# Revit family: Edge_TB42_C_Side_Hung_Standard
name_source: partatom
category: Windows
revit_build: Autodesk Revit 2014 (Build: 20130308_1515(x64)
units: mm (PartAtom-declared; Revit-internal decimal feet)

## types (12) — shared parameters
Aluminium Thickness = 1 mm  [stored 0.00328084 ft]
Bead SG Gap = 13 mm
Casement Dimension = 42 mm  [stored 0.137795 ft]
Custom Sash Left Width = 554 mm  [stored 1.81759 ft]
Custom Sash Right Width = 554 mm  [stored 1.81759 ft]
DG Extrusion Start = 11 mm  [stored 0.0360892 ft]
DG Gasket Finish = Double Glazing Gasket Material
DG Thickness Calc = 4 mm  [stored 0.0131234 ft]
Default Sill Height = 800 mm  [stored 2.62467 ft]
Depth Bead = 28 mm  [stored 0.0918635 ft]
Depth Mullion = 43 mm  [stored 0.141076 ft]
Description = Thermal break casement windows (42mm), Type C side hung
Frame Center Offset = 21 mm  [stored 0.0688976 ft]
Limit Fixed Pane Width Max = 1500 mm  [stored 4.92126 ft]
Limit Fixed Pane Width Min = 200 mm  [stored 0.656168 ft]
Limit Sash Height Max = 1500 mm  [stored 4.92126 ft]
Limit Sash Height Min = 300 mm  [stored 0.984252 ft]
Limit Sash Width Max = 700 mm  [stored 2.29659 ft]
Limit Sash Width Min = 300 mm  [stored 0.984252 ft]
Limit Window Height Max = 1546 mm
Limit Window Height Min = 346 mm
Limit Window Width Max = 2700 mm
Limit Window Width Min = 1400 mm
Manufacturer = Crealco
Max System DG One Piece Thickness = 6 mm  [stored 0.019685 ft]
Max System DG Unit Thickness = 25 mm  [stored 0.082021 ft]
Model = Edge
Offset Bead Center Reversed = 21 mm  [stored 0.0688976 ft]
Offset Fixed Panel Left = 600 mm  [stored 1.9685 ft]
Offset Mullion Left Side = 570 mm  [stored 1.87008 ft]
Offset Mullion Right Side = 570 mm  [stored 1.87008 ft]
Offset Sash Side = 23 mm  [stored 0.0754593 ft]
Offset Sash Top = 23 mm  [stored 0.0754593 ft]
Offset Window Exterior = 21 mm  [stored 0.0688976 ft]
SG Gasket Thickness = 6 mm  [stored 0.019685 ft]
Sash Center Offset = 18 mm
Sash Overlap = 7 mm  [stored 0.0229659 ft]
Sash Spacing Inner = 8 mm  [stored 0.0262467 ft]
Side Hung Left = Yes
Side Hung Right = No
URL = http://www.crealco.co.za
Wall Closure = By host
Width Bead = 15 mm  [stored 0.0492126 ft]
Width Profile = 30 mm  [stored 0.0984252 ft]
Width Sash Left = 554 mm  [stored 1.81759 ft]
Width Sash Left Opening = 524 mm  [stored 1.71916 ft]
Width Sash Right = 554 mm  [stored 1.81759 ft]
Width Sash Right Opening = 524 mm  [stored 1.71916 ft]
zero-valued in all types: Window Exterior Offset

## per-type parameters (varying)
- EDGE-1809SS-1000Pa: Area Pane Left=0.35 m²; Area Pane Middle=0.48 m²; Area Pane Right=0.35 m²; Clearvue Insulated LowE SHGC Value=0.461; Clearvue Insulated LowE U Value=2.6; Clearvue Insulated SHGC Value=0.507; Clearvue Insulated U Value=3.09; Clearvue SHGC Value=0.564; Clearvue U Value=5.33; Custom Windload=1000 mm  [stored 3.28084 ft]; Custom Window Height=890 mm  [stored 2.91995 ft]; Custom Window Width=1790 mm; Energy Advantage SHGC Value=0.505; Energy Advantage U Value=3.96; Has Stiffener Cap=No; Height=890 mm  [stored 2.91995 ft]; Height Fixed Panel Center=830 mm  [stored 2.7231 ft]; Height Sash=814 mm  [stored 2.6706 ft]; Height Sash Opening=844 mm  [stored 2.76903 ft]; Intruderprufe Insulated LowE SHGC Value=0.419; Intruderprufe Insulated LowE U Value=2.56; Intruderprufe Insulated SHGC Value=0.465; Intruderprufe Insulated U Value=3.05; Intruderprufe LowE SHGC Value=0.471; Intruderprufe LowE U Value=3.96; Intruderprufe SHGC Value=0.526; Intruderprufe U Value=5.24; Length Mullion=890 mm  [stored 2.91995 ft]; Max Pane Area=0.48 m²; Mullion Depth Windload Based=0 mm  [stored 0 ft]; Sash Height=845 mm  [stored 2.77231 ft]; Width=1790 mm; Width Fixed Panel Center=590 mm; Windload Design=1000 mm  [stored 3.28084 ft]
- EDGE-2409SS-1000Pa: Area Pane Left=0.35 m²; Area Pane Middle=0.97 m²; Area Pane Right=0.35 m²; Clearvue Insulated LowE SHGC Value=0.499; Clearvue Insulated LowE U Value=2.49; Clearvue Insulated SHGC Value=0.549; Clearvue Insulated U Value=3.03; Clearvue SHGC Value=0.612; Clearvue U Value=5.43; Custom Windload=1000 mm  [stored 3.28084 ft]; Custom Window Height=890 mm  [stored 2.91995 ft]; Custom Window Width=2390 mm; Energy Advantage SHGC Value=0.548; Energy Advantage U Value=3.92; Has Stiffener Cap=No; Height=890 mm  [stored 2.91995 ft]; Height Fixed Panel Center=830 mm  [stored 2.7231 ft]; Height Sash=814 mm  [stored 2.6706 ft]; Height Sash Opening=844 mm  [stored 2.76903 ft]; Intruderprufe Insulated LowE SHGC Value=0.455; Intruderprufe Insulated LowE U Value=2.45; Intruderprufe Insulated SHGC Value=0.504; Intruderprufe Insulated U Value=2.98; Intruderprufe LowE SHGC Value=0.511; Intruderprufe LowE U Value=3.91; Intruderprufe SHGC Value=0.572; Intruderprufe U Value=5.3; Length Mullion=890 mm  [stored 2.91995 ft]; Max Pane Area=0.97 m²; Mullion Depth Windload Based=0 mm  [stored 0 ft]; Sash Height=845 mm  [stored 2.77231 ft]; Width=2390 mm; Width Fixed Panel Center=1190 mm  [stored 3.9042 ft]; Windload Design=1000 mm  [stored 3.28084 ft]
- EDGE-1812SS-1000Pa: Area Pane Left=0.49 m²; Area Pane Middle=0.65 m²; Area Pane Right=0.49 m²; Clearvue Insulated LowE SHGC Value=0.481; Clearvue Insulated LowE U Value=2.54; Clearvue Insulated SHGC Value=0.529; Clearvue Insulated U Value=6.05; Clearvue SHGC Value=0.591; Clearvue U Value=5.38; Custom Windload=1000 mm  [stored 3.28084 ft]; Custom Window Height=1190 mm  [stored 3.9042 ft]; Custom Window Width=1790 mm; Energy Advantage SHGC Value=0.528; Energy Advantage U Value=3.94; Has Stiffener Cap=No; Height=1190 mm  [stored 3.9042 ft]; Height Fixed Panel Center=1130 mm  [stored 3.70735 ft]; Height Sash=1114 mm  [stored 3.65486 ft]; Height Sash Opening=1144 mm  [stored 3.75328 ft]; Intruderprufe Insulated LowE SHGC Value=0.486; Intruderprufe Insulated LowE U Value=3.01; Intruderprufe Insulated SHGC Value=0.438; Intruderprufe Insulated U Value=2.5; Intruderprufe LowE SHGC Value=0.493; Intruderprufe LowE U Value=3.93; Intruderprufe SHGC Value=0.552; Intruderprufe U Value=5.29; Length Mullion=1190 mm  [stored 3.9042 ft]; Max Pane Area=0.65 m²; Mullion Depth Windload Based=0 mm  [stored 0 ft]; Sash Height=1145 mm  [stored 3.75656 ft]; Width=1790 mm; Width Fixed Panel Center=590 mm; Windload Design=1000 mm  [stored 3.28084 ft]
- EDGE-2412SS-1000Pa: Area Pane Left=0.49 m²; Area Pane Middle=1.32 m²; Area Pane Right=0.49 m²; Clearvue Insulated LowE SHGC Value=0.519; Clearvue Insulated LowE U Value=2.42; Clearvue Insulated SHGC Value=0.57; Clearvue Insulated U Value=2.99; Clearvue SHGC Value=0.638; Clearvue U Value=5.48; Custom Windload=1000 mm  [stored 3.28084 ft]; Custom Window Height=1190 mm  [stored 3.9042 ft]; Custom Window Width=2390 mm; Energy Advantage SHGC Value=0.571; Energy Advantage U Value=3.9; Has Stiffener Cap=No; Height=1190 mm  [stored 3.9042 ft]; Height Fixed Panel Center=1130 mm  [stored 3.70735 ft]; Height Sash=1114 mm  [stored 3.65486 ft]; Height Sash Opening=1144 mm  [stored 3.75328 ft]; Intruderprufe Insulated LowE SHGC Value=0.473; Intruderprufe Insulated LowE U Value=2.39; Intruderprufe Insulated SHGC Value=0.524; Intruderprufe Insulated U Value=2.95; Intruderprufe LowE SHGC Value=0.532; Intruderprufe LowE U Value=3.88; Intruderprufe SHGC Value=0.597; Intruderprufe U Value=5.38; Length Mullion=1190 mm  [stored 3.9042 ft]; Max Pane Area=1.32 m²; Mullion Depth Windload Based=0 mm  [stored 0 ft]; Sash Height=1145 mm  [stored 3.75656 ft]; Width=2390 mm; Width Fixed Panel Center=1190 mm  [stored 3.9042 ft]; Windload Design=1000 mm  [stored 3.28084 ft]
- EDGE-1809SS-1500Pa: Area Pane Left=0.35 m²; Area Pane Middle=0.48 m²; Area Pane Right=0.35 m²; Clearvue Insulated LowE SHGC Value=0.461; Clearvue Insulated LowE U Value=2.6; Clearvue Insulated SHGC Value=0.507; Clearvue Insulated U Value=3.09; Clearvue SHGC Value=0.564; Clearvue U Value=5.33; Custom Windload=1500 mm  [stored 4.92126 ft]; Custom Window Height=890 mm  [stored 2.91995 ft]; Custom Window Width=1790 mm; Energy Advantage SHGC Value=0.505; Energy Advantage U Value=3.96; Has Stiffener Cap=No; Height=890 mm  [stored 2.91995 ft]; Height Fixed Panel Center=830 mm  [stored 2.7231 ft]; Height Sash=814 mm  [stored 2.6706 ft]; Height Sash Opening=844 mm  [stored 2.76903 ft]; Intruderprufe Insulated LowE SHGC Value=0.419; Intruderprufe Insulated LowE U Value=2.56; Intruderprufe Insulated SHGC Value=0.465; Intruderprufe Insulated U Value=3.05; Intruderprufe LowE SHGC Value=0.471; Intruderprufe LowE U Value=3.96; Intruderprufe SHGC Value=0.526; Intruderprufe U Value=5.24; Length Mullion=890 mm  [stored 2.91995 ft]; Max Pane Area=0.48 m²; Mullion Depth Windload Based=0 mm  [stored 0 ft]; Sash Height=845 mm  [stored 2.77231 ft]; Width=1790 mm; Width Fixed Panel Center=590 mm; Windload Design=1500 mm  [stored 4.92126 ft]
- EDGE-1809SS-2000Pa: Area Pane Left=0.35 m²; Area Pane Middle=0.48 m²; Area Pane Right=0.35 m²; Clearvue Insulated LowE SHGC Value=0.461; Clearvue Insulated LowE U Value=2.6; Clearvue Insulated SHGC Value=0.507; Clearvue Insulated U Value=3.09; Clearvue SHGC Value=0.564; Clearvue U Value=5.33; Custom Windload=2000 mm; Custom Window Height=890 mm  [stored 2.91995 ft]; Custom Window Width=1790 mm; Energy Advantage SHGC Value=0.505; Energy Advantage U Value=3.96; Has Stiffener Cap=No; Height=890 mm  [stored 2.91995 ft]; Height Fixed Panel Center=830 mm  [stored 2.7231 ft]; Height Sash=814 mm  [stored 2.6706 ft]; Height Sash Opening=844 mm  [stored 2.76903 ft]; Intruderprufe Insulated LowE SHGC Value=0.419; Intruderprufe Insulated LowE U Value=2.56; Intruderprufe Insulated SHGC Value=0.465; Intruderprufe Insulated U Value=3.05; Intruderprufe LowE SHGC Value=0.471; Intruderprufe LowE U Value=3.96; Intruderprufe SHGC Value=0.526; Intruderprufe U Value=5.24; Length Mullion=890 mm  [stored 2.91995 ft]; Max Pane Area=0.48 m²; Mullion Depth Windload Based=0 mm  [stored 0 ft]; Sash Height=845 mm  [stored 2.77231 ft]; Width=1790 mm; Width Fixed Panel Center=590 mm; Windload Design=2000 mm
- EDGE-2409SS-1500Pa: Area Pane Left=0.35 m²; Area Pane Middle=0.97 m²; Area Pane Right=0.35 m²; Clearvue Insulated LowE SHGC Value=0.499; Clearvue Insulated LowE U Value=2.49; Clearvue Insulated SHGC Value=0.549; Clearvue Insulated U Value=3.03; Clearvue SHGC Value=0.612; Clearvue U Value=5.43; Custom Windload=1500 mm  [stored 4.92126 ft]; Custom Window Height=890 mm  [stored 2.91995 ft]; Custom Window Width=2390 mm; Energy Advantage SHGC Value=0.548; Energy Advantage U Value=3.92; Has Stiffener Cap=No; Height=890 mm  [stored 2.91995 ft]; Height Fixed Panel Center=830 mm  [stored 2.7231 ft]; Height Sash=814 mm  [stored 2.6706 ft]; Height Sash Opening=844 mm  [stored 2.76903 ft]; Intruderprufe Insulated LowE SHGC Value=0.455; Intruderprufe Insulated LowE U Value=2.45; Intruderprufe Insulated SHGC Value=0.504; Intruderprufe Insulated U Value=2.98; Intruderprufe LowE SHGC Value=0.511; Intruderprufe LowE U Value=3.91; Intruderprufe SHGC Value=0.572; Intruderprufe U Value=5.3; Length Mullion=890 mm  [stored 2.91995 ft]; Max Pane Area=0.97 m²; Mullion Depth Windload Based=0 mm  [stored 0 ft]; Sash Height=845 mm  [stored 2.77231 ft]; Width=2390 mm; Width Fixed Panel Center=1190 mm  [stored 3.9042 ft]; Windload Design=1500 mm  [stored 4.92126 ft]
- EDGE-2409SS-2000Pa: Area Pane Left=0.35 m²; Area Pane Middle=0.97 m²; Area Pane Right=0.35 m²; Clearvue Insulated LowE SHGC Value=0.499; Clearvue Insulated LowE U Value=2.49; Clearvue Insulated SHGC Value=0.549; Clearvue Insulated U Value=3.03; Clearvue SHGC Value=0.612; Clearvue U Value=5.43; Custom Windload=2000 mm; Custom Window Height=890 mm  [stored 2.91995 ft]; Custom Window Width=2390 mm; Energy Advantage SHGC Value=0.548; Energy Advantage U Value=3.92; Has Stiffener Cap=No; Height=890 mm  [stored 2.91995 ft]; Height Fixed Panel Center=830 mm  [stored 2.7231 ft]; Height Sash=814 mm  [stored 2.6706 ft]; Height Sash Opening=844 mm  [stored 2.76903 ft]; Intruderprufe Insulated LowE SHGC Value=0.455; Intruderprufe Insulated LowE U Value=2.45; Intruderprufe Insulated SHGC Value=0.504; Intruderprufe Insulated U Value=2.98; Intruderprufe LowE SHGC Value=0.511; Intruderprufe LowE U Value=3.91; Intruderprufe SHGC Value=0.572; Intruderprufe U Value=5.3; Length Mullion=890 mm  [stored 2.91995 ft]; Max Pane Area=0.97 m²; Mullion Depth Windload Based=0 mm  [stored 0 ft]; Sash Height=845 mm  [stored 2.77231 ft]; Width=2390 mm; Width Fixed Panel Center=1190 mm  [stored 3.9042 ft]; Windload Design=2000 mm
- EDGE-1812SS-1500Pa: Area Pane Left=0.49 m²; Area Pane Middle=0.65 m²; Area Pane Right=0.49 m²; Clearvue Insulated LowE SHGC Value=0.481; Clearvue Insulated LowE U Value=2.54; Clearvue Insulated SHGC Value=0.529; Clearvue Insulated U Value=6.05; Clearvue SHGC Value=0.591; Clearvue U Value=5.38; Custom Windload=1500 mm  [stored 4.92126 ft]; Custom Window Height=1190 mm  [stored 3.9042 ft]; Custom Window Width=1790 mm; Energy Advantage SHGC Value=0.528; Energy Advantage U Value=3.94; Has Stiffener Cap=No; Height=1190 mm  [stored 3.9042 ft]; Height Fixed Panel Center=1130 mm  [stored 3.70735 ft]; Height Sash=1114 mm  [stored 3.65486 ft]; Height Sash Opening=1144 mm  [stored 3.75328 ft]; Intruderprufe Insulated LowE SHGC Value=0.486; Intruderprufe Insulated LowE U Value=3.01; Intruderprufe Insulated SHGC Value=0.438; Intruderprufe Insulated U Value=2.5; Intruderprufe LowE SHGC Value=0.493; Intruderprufe LowE U Value=3.93; Intruderprufe SHGC Value=0.552; Intruderprufe U Value=5.29; Length Mullion=1190 mm  [stored 3.9042 ft]; Max Pane Area=0.65 m²; Mullion Depth Windload Based=0 mm  [stored 0 ft]; Sash Height=1145 mm  [stored 3.75656 ft]; Width=1790 mm; Width Fixed Panel Center=590 mm; Windload Design=1500 mm  [stored 4.92126 ft]
- EDGE-1812SS-2000Pa: Area Pane Left=0.49 m²; Area Pane Middle=0.65 m²; Area Pane Right=0.49 m²; Clearvue Insulated LowE SHGC Value=0.551; Clearvue Insulated LowE U Value=2.07; Clearvue Insulated SHGC Value=0.606; Clearvue Insulated U Value=2.6; Clearvue SHGC Value=0.678; Clearvue U Value=4.79; Custom Windload=2000 mm; Custom Window Height=1190 mm  [stored 3.9042 ft]; Custom Window Width=1790 mm; Energy Advantage SHGC Value=0.605; Energy Advantage U Value=3.35; Has Stiffener Cap=Yes; Height=1190 mm  [stored 3.9042 ft]; Height Fixed Panel Center=1130 mm  [stored 3.70735 ft]; Height Sash=1114 mm  [stored 3.65486 ft]; Height Sash Opening=1144 mm  [stored 3.75328 ft]; Intruderprufe Insulated LowE SHGC Value=0.502; Intruderprufe Insulated LowE U Value=2.03; Intruderprufe Insulated SHGC Value=0.558; Intruderprufe Insulated U Value=2.55; Intruderprufe LowE SHGC Value=0.564; Intruderprufe LowE U Value=3.32; Intruderprufe SHGC Value=0.635; Intruderprufe U Value=4.7; Length Mullion=1190 mm  [stored 3.9042 ft]; Max Pane Area=0.65 m²; Mullion Depth Windload Based=1 mm  [stored 0.00328084 ft]; Sash Height=1145 mm  [stored 3.75656 ft]; Width=1790 mm; Width Fixed Panel Center=590 mm; Windload Design=2000 mm
- EDGE-2412SS-1500Pa: Area Pane Left=0.49 m²; Area Pane Middle=1.32 m²; Area Pane Right=0.49 m²; Clearvue Insulated LowE SHGC Value=0.519; Clearvue Insulated LowE U Value=2.42; Clearvue Insulated SHGC Value=0.57; Clearvue Insulated U Value=2.99; Clearvue SHGC Value=0.638; Clearvue U Value=5.48; Custom Windload=1500 mm  [stored 4.92126 ft]; Custom Window Height=1190 mm  [stored 3.9042 ft]; Custom Window Width=2390 mm; Energy Advantage SHGC Value=0.571; Energy Advantage U Value=3.9; Has Stiffener Cap=No; Height=1190 mm  [stored 3.9042 ft]; Height Fixed Panel Center=1130 mm  [stored 3.70735 ft]; Height Sash=1114 mm  [stored 3.65486 ft]; Height Sash Opening=1144 mm  [stored 3.75328 ft]; Intruderprufe Insulated LowE SHGC Value=0.473; Intruderprufe Insulated LowE U Value=2.39; Intruderprufe Insulated SHGC Value=0.524; Intruderprufe Insulated U Value=2.95; Intruderprufe LowE SHGC Value=0.532; Intruderprufe LowE U Value=3.88; Intruderprufe SHGC Value=0.597; Intruderprufe U Value=5.38; Length Mullion=1190 mm  [stored 3.9042 ft]; Max Pane Area=1.32 m²; Mullion Depth Windload Based=0 mm  [stored 0 ft]; Sash Height=1145 mm  [stored 3.75656 ft]; Width=2390 mm; Width Fixed Panel Center=1190 mm  [stored 3.9042 ft]; Windload Design=1500 mm  [stored 4.92126 ft]
- EDGE-2412SS-2000Pa: Area Pane Left=0.49 m²; Area Pane Middle=1.32 m²; Area Pane Right=0.49 m²; Clearvue Insulated LowE SHGC Value=0.571; Clearvue Insulated LowE U Value=0.207; Clearvue Insulated SHGC Value=0.628; Clearvue Insulated U Value=2.65; Clearvue SHGC Value=0.704; Clearvue U Value=5.04; Custom Windload=2000 mm; Custom Window Height=1190 mm  [stored 3.9042 ft]; Custom Window Width=2390 mm; Energy Advantage SHGC Value=0.628; Energy Advantage U Value=3.46; Has Stiffener Cap=Yes; Height=1190 mm  [stored 3.9042 ft]; Height Fixed Panel Center=1130 mm  [stored 3.70735 ft]; Height Sash=1114 mm  [stored 3.65486 ft]; Height Sash Opening=1144 mm  [stored 3.75328 ft]; Intruderprufe Insulated LowE SHGC Value=0.521; Intruderprufe Insulated LowE U Value=2.04; Intruderprufe Insulated SHGC Value=0.578; Intruderprufe Insulated U Value=2.61; Intruderprufe LowE SHGC Value=0.585; Intruderprufe LowE U Value=3.42; Intruderprufe SHGC Value=0.659; Intruderprufe U Value=4.94; Length Mullion=1190 mm  [stored 3.9042 ft]; Max Pane Area=1.32 m²; Mullion Depth Windload Based=1 mm  [stored 0.00328084 ft]; Sash Height=1145 mm  [stored 3.75656 ft]; Width=2390 mm; Width Fixed Panel Center=1190 mm  [stored 3.9042 ft]; Windload Design=2000 mm

note: [stored X ft] marks values corroborated as IEEE doubles in the binary element streams (Revit-internal decimal feet)

## geometry (parser evidence)
native form markers: Extrusion x1, Sweep x25
no freeform markers — native parametric forms only
